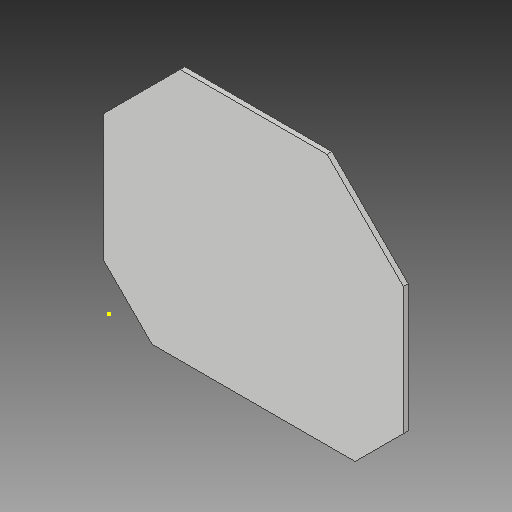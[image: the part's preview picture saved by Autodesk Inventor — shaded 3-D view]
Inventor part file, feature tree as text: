
AUTODESK INVENTOR PART (.ipt)
format: ipt  version: 2017 (Build 210142000, 142)  size: 103,424 bytes
history: native  units: in
note: dims shown in document units (in); Inventor stores cm internally (conversion verified against a paired STEP export)
features: chamfer x4, sketch x2, extrude x1, direct_edit x1, move_body x1
ambient origin geometry x8: Origin, YZ Plane, XZ Plane, XY Plane, X Axis, Y Axis, Z Axis, Center Point
bodies: Solid1 (feature_tree)
feature tree (9):
  extrude  "Extrusion1"  Depth=6.957in
  chamfer  "Chamfer1"  Distance=0.15in
  chamfer  "Chamfer2"  Distance=1.5in Angle=45.0deg
  chamfer  "Chamfer3"  Distance=1.5in Angle=45.0deg
  chamfer  "Chamfer4"  Distance=1.5in Angle=45.0deg
  direct_edit  "Direct Edit1"
  sketch  "Sketch2"  dims[d13=1.5in d14=0.125in d15=45.0deg d16=0.0in d17=0.0in d18=0.87in]
  sketch  "Sketch1"  dims[d0=9.308in d1=6.957in d2=0.15in d3=0.0in d4=1.5in d5=0.125in d6=45.0deg d7=1.5in d8=0.125in d9=45.0deg d10=1.5in d11=0.125in d12=45.0deg]
  move_body  "Move1"
